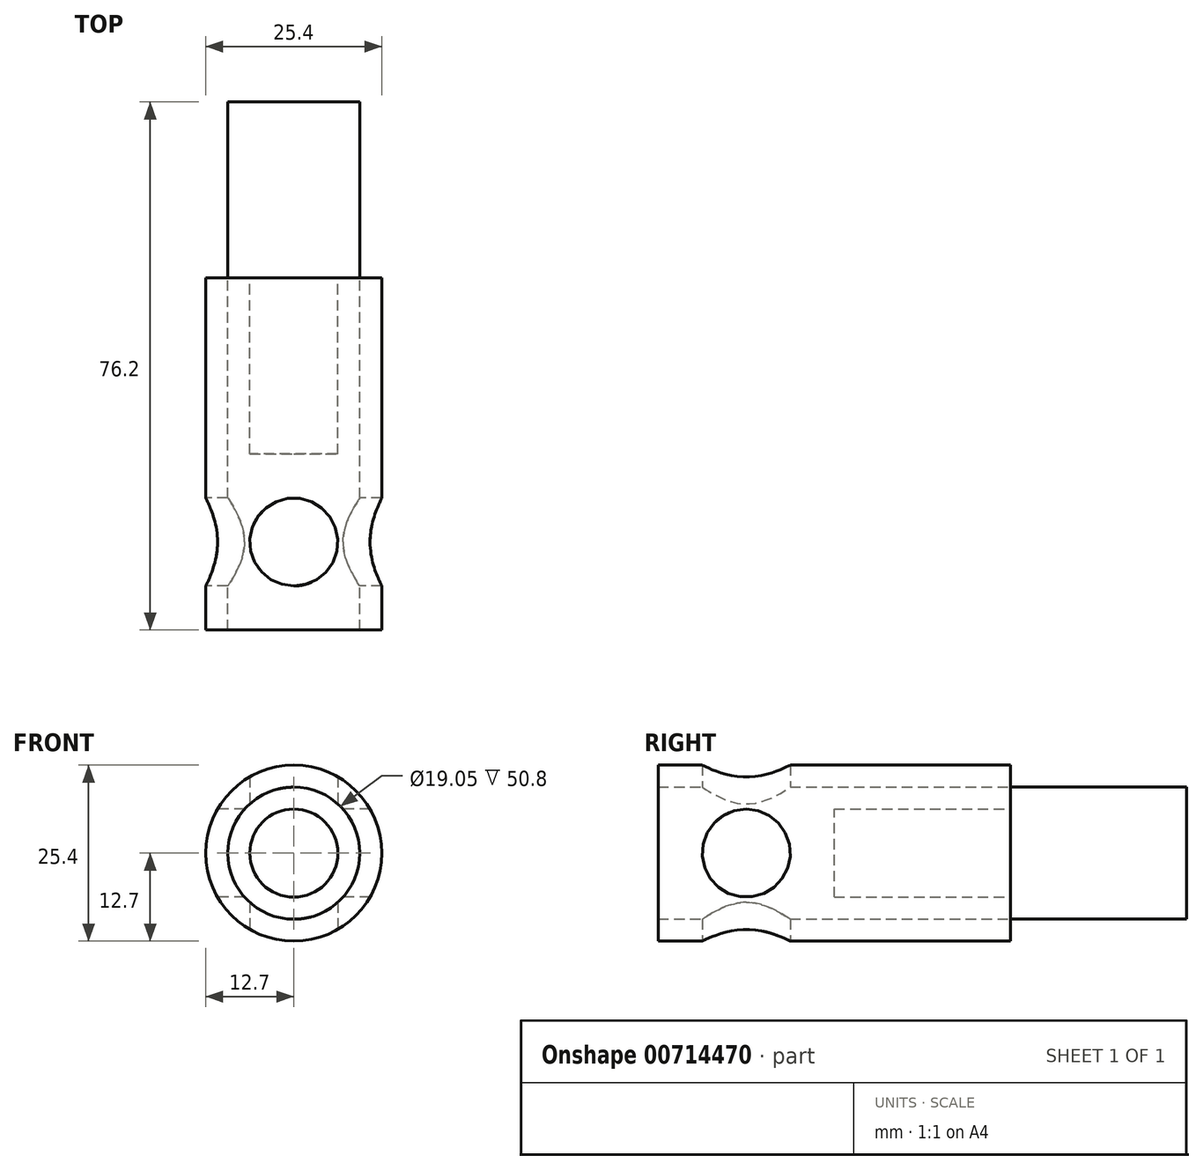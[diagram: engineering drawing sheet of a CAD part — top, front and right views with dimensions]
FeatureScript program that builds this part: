
annotation { "Feature Type Name" : "Feature", "Feature Type Description" : "" }
export const myFeature = defineFeature(function(context is Context, id is Id, definition is map)
    precondition{}
    {
        {
            var Q0;
            Q0=qCreatedBy(makeId("Front.planeOp"),FACE);
            var sketch = newSketch(context, id + "F0", { "sketchPlane" : qUnion([Q0])});
            skCircle(sketch, "E0", {"center": v(0, 0) * mm, "radius": 9.53 * mm});
            skCircle(sketch, "E1", {"center": v(0, 0) * mm, "radius": 12.7 * mm});
            skCircle(sketch, "E2", {"center": v(0, 0) * mm, "radius": 6.35 * mm});
            skSolve(sketch);
        }
        {
            var Q0;
            Q0=makeQuery(id+"F0.imprint","IMPRINT",FACE,{"disambiguationData":[TD([[makeQuery(id+"F0.imprint","IMPRINT",EDGE,{"derivedFrom":sQuery(id+"F0.wireOp",EDGE,"E0")}),-1.0]])]});
            extrude(context, id + "F1", {"entities" : qUnion([Q0]), "depth" : 50.8 * mm, "offsetDistance" : 25.4 * mm});
        }
        {
            var Q0;
            Q0=qCreatedBy(makeId("Right.planeOp"),FACE);
            var sketch = newSketch(context, id + "F2", { "sketchPlane" : qUnion([Q0])});
            skCircle(sketch, "E3", {"center": v(-38.1, 0) * mm, "radius": 6.35 * mm});
            skLineSegment(sketch, "E4", {"start": v(-38.1, 0) * mm, "end": v(0, 0) * mm, "construction": true});
            skSolve(sketch);
        }
        {
            var Q0;
            Q0=makeQuery(id+"F2.imprint","IMPRINT",FACE,{"disambiguationData":[TD([[makeQuery(id+"F2.imprint","IMPRINT",EDGE,{"derivedFrom":sQuery(id+"F2.wireOp",EDGE,"E3")}),1.0]])]});
            extrude(context, id + "F3", {"entities" : qUnion([Q0]), "operationType" : NewBodyOperationType.REMOVE, "endBound" : BoundingType.THROUGH_ALL, "depth" : 25.4 * mm, "offsetDistance" : 25.4 * mm, "hasSecondDirection" : true, "secondDirectionBound" : SecondDirectionBoundingType.THROUGH_ALL, "secondDirectionOppositeDirection" : true, "secondDirectionDepth" : 25.4 * mm});
        }
        {
            var Q0;
            Q0=qCreatedBy(makeId("Top.planeOp"),FACE);
            var sketch = newSketch(context, id + "F4", { "sketchPlane" : qUnion([Q0])});
            skCircle(sketch, "E5", {"center": v(0, -38.1) * mm, "radius": 6.35 * mm});
            skLineSegment(sketch, "E6", {"start": v(0, -38.1) * mm, "end": v(0, 0) * mm, "construction": true});
            skSolve(sketch);
        }
        {
            var Q0;
            Q0=makeQuery(id+"F4.imprint","IMPRINT",FACE,{"disambiguationData":[TD([[makeQuery(id+"F4.imprint","IMPRINT",EDGE,{"derivedFrom":sQuery(id+"F4.wireOp",EDGE,"E5")}),1.0]])]});
            extrude(context, id + "F5", {"entities" : qUnion([Q0]), "operationType" : NewBodyOperationType.REMOVE, "endBound" : BoundingType.THROUGH_ALL, "depth" : 25.4 * mm, "offsetDistance" : 25.4 * mm, "hasSecondDirection" : true, "secondDirectionBound" : SecondDirectionBoundingType.THROUGH_ALL, "secondDirectionOppositeDirection" : true, "secondDirectionDepth" : 25.4 * mm});
        }
        {
            var Q0;
            Q0=makeQuery(id+"F0.imprint","IMPRINT",FACE,{"disambiguationData":[TD([[makeQuery(id+"F0.imprint","IMPRINT",EDGE,{"derivedFrom":sQuery(id+"F0.wireOp",EDGE,"E0")}),1.0]])]});
            var Q1;
            Q1=makeQuery(id+"F0.imprint","IMPRINT",FACE,{"disambiguationData":[TD([[makeQuery(id+"F0.imprint","IMPRINT",EDGE,{"derivedFrom":sQuery(id+"F0.wireOp",EDGE,"E2")}),1.0]])]});
            extrude(context, id + "F6", {"entities" : qUnion([Q0, Q1]), "oppositeDirection" : true, "depth" : 25.4 * mm, "offsetDistance" : 25.4 * mm});
        }
        {
            var Q0;
            Q0=makeQuery(id+"F0.imprint","IMPRINT",FACE,{"disambiguationData":[TD([[makeQuery(id+"F0.imprint","IMPRINT",EDGE,{"derivedFrom":sQuery(id+"F0.wireOp",EDGE,"E2")}),1.0]])]});
            extrude(context, id + "F7", {"entities" : qUnion([Q0]), "operationType" : NewBodyOperationType.ADD, "depth" : 25.4 * mm, "offsetDistance" : 25.4 * mm});
        }
    });
